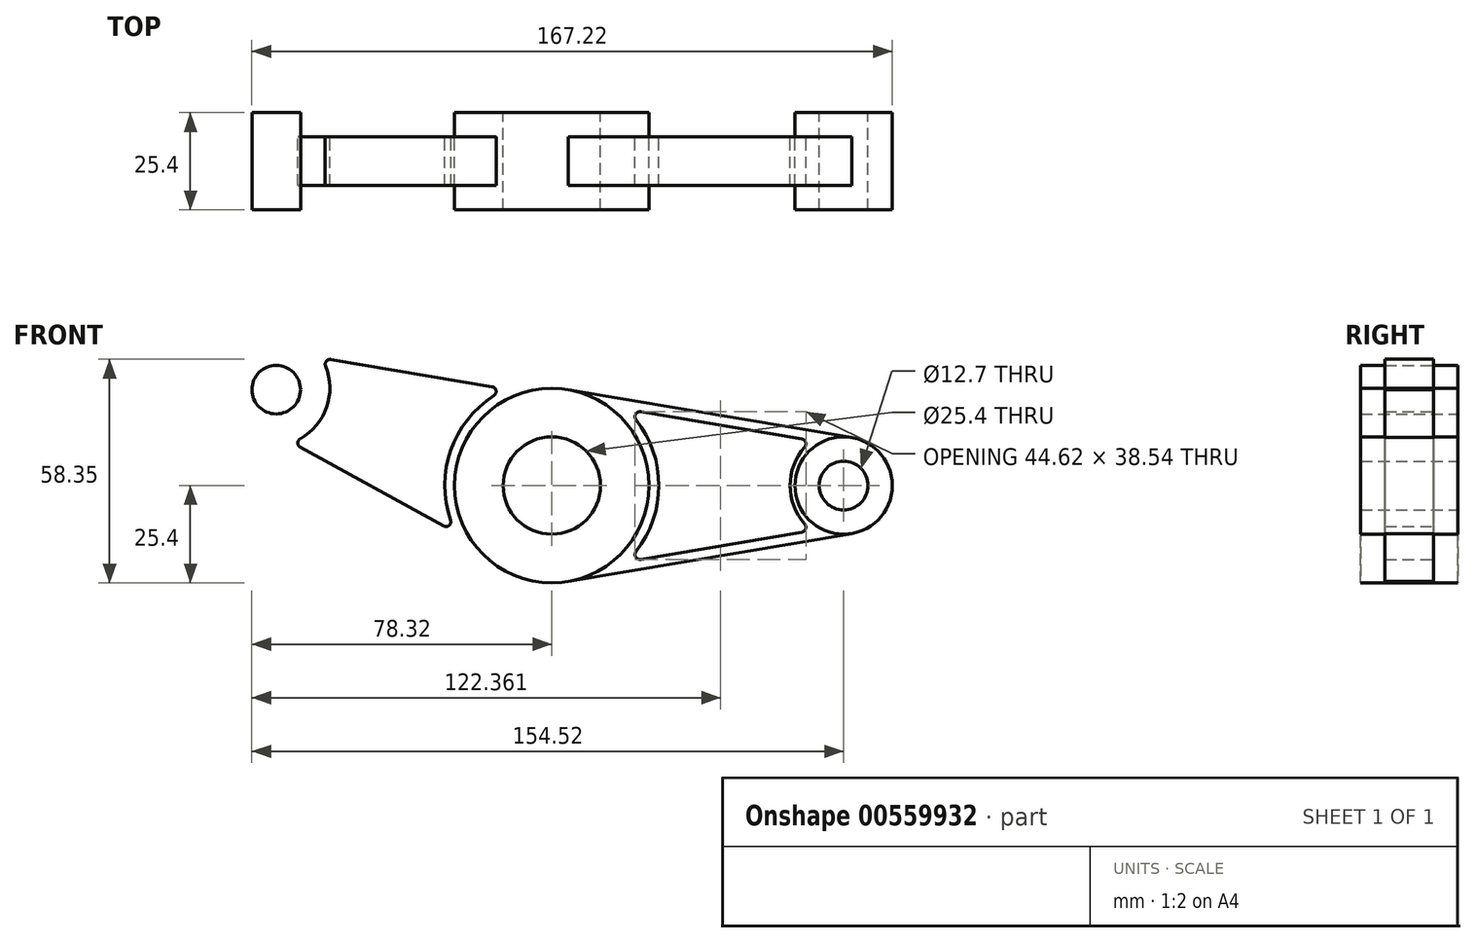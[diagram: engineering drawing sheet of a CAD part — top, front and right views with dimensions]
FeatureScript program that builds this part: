
annotation { "Feature Type Name" : "Feature", "Feature Type Description" : "" }
export const myFeature = defineFeature(function(context is Context, id is Id, definition is map)
    precondition{}
    {
        {
            var Q0;
            Q0=qCreatedBy(makeId("Front.planeOp"),FACE);
            var sketch = newSketch(context, id + "F0", { "sketchPlane" : qUnion([Q0])});
            skCircle(sketch, "E0", {"center": v(0, 0) * mm, "radius": 25.4 * mm});
            skCircle(sketch, "E1", {"center": v(76.2, 0) * mm, "radius": 12.7 * mm});
            skCircle(sketch, "E2", {"center": v(0, 0) * mm, "radius": 12.7 * mm});
            skCircle(sketch, "E3", {"center": v(76.2, 0) * mm, "radius": 6.35 * mm});
            skLineSegment(sketch, "E4", {"start": v(4.23, -25.04) * mm, "end": v(78.32, -12.52) * mm});
            skLineSegment(sketch, "E5", {"start": v(4.23, 25.04) * mm, "end": v(78.32, 12.52) * mm});
            skLineSegment(sketch, "E6.0", {"start": v(23.2, 19.26) * mm, "end": v(65.3, 12.15) * mm});
            skArc(sketch, "E7.0", {"start": v(22, -17.23) * mm, "mid": v(27.94, 0) * mm, "end": v(22, 17.23) * mm});
            skLineSegment(sketch, "E8.0", {"start": v(23.2, -19.26) * mm, "end": v(65.3, -12.15) * mm});
            skArc(sketch, "E9.trimOffspring", {"start": v(66.04, 10.06) * mm, "mid": v(62.25, 0) * mm, "end": v(66.04, -10.06) * mm});
            skPoint(sketch, "E10.visualSharp", {"position": v(19.65, 19.86) * mm});
            skArc(sketch, "E10.filletArc", {"start": v(23.2, 19.26) * mm, "mid": v(21.9, 18.66) * mm, "end": v(22, 17.23) * mm});
            skPoint(sketch, "E11.visualSharp", {"position": v(67.76, 11.73) * mm});
            skArc(sketch, "E11.filletArc", {"start": v(66.04, 10.06) * mm, "mid": v(66.28, 11.32) * mm, "end": v(65.3, 12.15) * mm});
            skPoint(sketch, "E12.visualSharp", {"position": v(67.76, -11.73) * mm});
            skArc(sketch, "E12.filletArc", {"start": v(65.3, -12.15) * mm, "mid": v(66.28, -11.32) * mm, "end": v(66.04, -10.06) * mm});
            skPoint(sketch, "E13.visualSharp", {"position": v(19.65, -19.86) * mm});
            skArc(sketch, "E13.filletArc", {"start": v(22, -17.23) * mm, "mid": v(21.9, -18.66) * mm, "end": v(23.2, -19.26) * mm});
            skArc(sketch, "E14.MirrorCS", {"start": v(-59.06, 31.2) * mm, "mid": v(-58.88, 32.48) * mm, "end": v(-57.68, 32.93) * mm});
            skArc(sketch, "E15.MirrorCS", {"start": v(-65.66, 9.99) * mm, "mid": v(-66.32, 11.1) * mm, "end": v(-65.68, 12.2) * mm});
            skArc(sketch, "E16.MirrorCS", {"start": v(-15.59, 25.82) * mm, "mid": v(-14.56, 24.82) * mm, "end": v(-15.11, 23.5) * mm});
            skArc(sketch, "E17.MirrorCS", {"start": v(-26.44, -9.04) * mm, "mid": v(-26.82, -10.42) * mm, "end": v(-28.25, -10.56) * mm});
            skCircle(sketch, "E18.MirrorC", {"center": v(-71.97, 25.04) * mm, "radius": 6.35 * mm});
            skPoint(sketch, "E19.MirrorP", {"position": v(-67.85, 11.2) * mm});
            skPoint(sketch, "E20.MirrorP", {"position": v(-12.03, 25.22) * mm});
            skCircle(sketch, "E21.MirrorC", {"center": v(-71.97, 25.04) * mm, "radius": 12.7 * mm});
            skPoint(sketch, "E22.MirrorP", {"position": v(-25.09, -12.3) * mm});
            skLineSegment(sketch, "E23.MirrorCS", {"start": v(-15.59, 25.82) * mm, "end": v(-57.68, 32.93) * mm});
            skArc(sketch, "E24.MirrorCS", {"start": v(-59.06, 31.2) * mm, "mid": v(-58.8, 20.46) * mm, "end": v(-65.68, 12.2) * mm});
            skPoint(sketch, "E25.MirrorP", {"position": v(-60.14, 33.35) * mm});
            skArc(sketch, "E26.MirrorCS", {"start": v(-26.44, -9.04) * mm, "mid": v(-26.39, 9.18) * mm, "end": v(-15.11, 23.5) * mm});
            skLineSegment(sketch, "E27.MirrorCS", {"start": v(-28.25, -10.56) * mm, "end": v(-65.66, 9.99) * mm});
            skLineSegment(sketch, "E28.MirrorCS", {"start": v(-12.23, -22.26) * mm, "end": v(-78.08, 13.91) * mm});
            skLineSegment(sketch, "E29.MirrorCS", {"start": v(4.23, 25.04) * mm, "end": v(-69.85, 37.57) * mm});
            skSolve(sketch);
        }
        {
            var Q0;
            Q0=makeQuery(id+"F0.imprint","IMPRINT",FACE,{"disambiguationData":[TD([[makeQuery(id+"F0.imprint","IMPRINT",EDGE,{"derivedFrom":sQuery(id+"F0.wireOp",EDGE,"E2")}),-1.0]])]});
            var Q1;
            Q1=makeQuery(id+"F0.imprint","IMPRINT",FACE,{"disambiguationData":[TD([[makeQuery(id+"F0.imprint","IMPRINT",EDGE,{"derivedFrom":sQuery(id+"F0.wireOp",EDGE,"E3")}),-1.0]])]});
            var Q2;
            Q2=makeQuery(id+"F0.imprint","IMPRINT",FACE,{"disambiguationData":[TD([[makeQuery(id+"F0.imprint","IMPRINT",EDGE,{"derivedFrom":sQuery(id+"F0.wireOp",EDGE,"E18.MirrorC")}),1.0]])]});
            extrude(context, id + "F1", {"entities" : qUnion([Q0, Q1, Q2]), "depth" : 25.4 * mm, "offsetDistance" : 25.4 * mm});
        }
        {
            var Q0;
            {var subQ1=sQuery(id+"F0.wireOp",EDGE,"E4");Q0=makeQuery(id+"F0.imprint","IMPRINT",FACE,{"disambiguationData":[TD([[makeQuery(id+"F0.imprint","IMPRINT",EDGE,{"derivedFrom":subQ1}),1.0]])]});}
            var Q1;
            Q1=makeQuery(id+"F0.imprint","IMPRINT",FACE,{"disambiguationData":[TD([[makeQuery(id+"F0.imprint","IMPRINT",EDGE,{"derivedFrom":sQuery(id+"F0.wireOp",EDGE,"E14.MirrorCS")}),1.0]])]});
            extrude(context, id + "F2", {"entities" : qUnion([Q0, Q1]), "depth" : 25.4 * mm, "offsetDistance" : 25.4 * mm});
        }
        {
            var Q0;
            {var subQ0=sQuery(id+"F0.wireOp",EDGE,"E4");Q0=makeQuery(id+"F0.imprint","IMPRINT",FACE,{"disambiguationData":[TD([[makeQuery(id+"F0.imprint","IMPRINT",EDGE,{"derivedFrom":subQ0}),1.0]])]});}
            var Q1;
            Q1=makeQuery(id+"F0.imprint","IMPRINT",FACE,{"disambiguationData":[TD([[makeQuery(id+"F0.imprint","IMPRINT",EDGE,{"derivedFrom":sQuery(id+"F0.wireOp",EDGE,"E14.MirrorCS")}),1.0]])]});
            extrude(context, id + "F3", {"entities" : qUnion([Q0, Q1]), "operationType" : NewBodyOperationType.REMOVE, "depth" : 6.35 * mm, "offsetDistance" : 25.4 * mm});
        }
        {
            var Q0;
            Q0=makeQuery(id+"F2.opExtrude","CAP_FACE",FACE,{"disambiguationData":[OSD([sQuery(id+"F0.wireOp",EDGE,"E14.MirrorCS"),sQuery(id+"F0.wireOp",EDGE,"E15.MirrorCS"),sQuery(id+"F0.wireOp",EDGE,"E16.MirrorCS"),sQuery(id+"F0.wireOp",EDGE,"E17.MirrorCS"),sQuery(id+"F0.wireOp",EDGE,"E21.MirrorC"),sQuery(id+"F0.wireOp",EDGE,"E23.MirrorCS"),sQuery(id+"F0.wireOp",EDGE,"E24.MirrorCS"),sQuery(id+"F0.wireOp",EDGE,"E26.MirrorCS"),sQuery(id+"F0.wireOp",EDGE,"E27.MirrorCS"),sQuery(id+"F0.wireOp",EDGE,"E0"),sQuery(id+"F0.wireOp",EDGE,"E28.MirrorCS"),sQuery(id+"F0.wireOp",EDGE,"E29.MirrorCS")])],"isStart":false});
            var Q1;
            Q1=makeQuery(id+"F2.opExtrude","CAP_FACE",FACE,{"disambiguationData":[OSD([sQuery(id+"F0.wireOp",EDGE,"E1"),sQuery(id+"F0.wireOp",EDGE,"E4"),sQuery(id+"F0.wireOp",EDGE,"E5"),sQuery(id+"F0.wireOp",EDGE,"E6.0"),sQuery(id+"F0.wireOp",EDGE,"E7.0"),sQuery(id+"F0.wireOp",EDGE,"E8.0"),sQuery(id+"F0.wireOp",EDGE,"E9.trimOffspring"),sQuery(id+"F0.wireOp",EDGE,"E10.filletArc"),sQuery(id+"F0.wireOp",EDGE,"E11.filletArc"),sQuery(id+"F0.wireOp",EDGE,"E12.filletArc"),sQuery(id+"F0.wireOp",EDGE,"E13.filletArc"),sQuery(id+"F0.wireOp",EDGE,"E0")])],"isStart":false});
            extrude(context, id + "F4", {"entities" : qUnion([Q0, Q1]), "operationType" : NewBodyOperationType.REMOVE, "oppositeDirection" : true, "depth" : 6.35 * mm, "offsetDistance" : 25.4 * mm});
        }
    });
